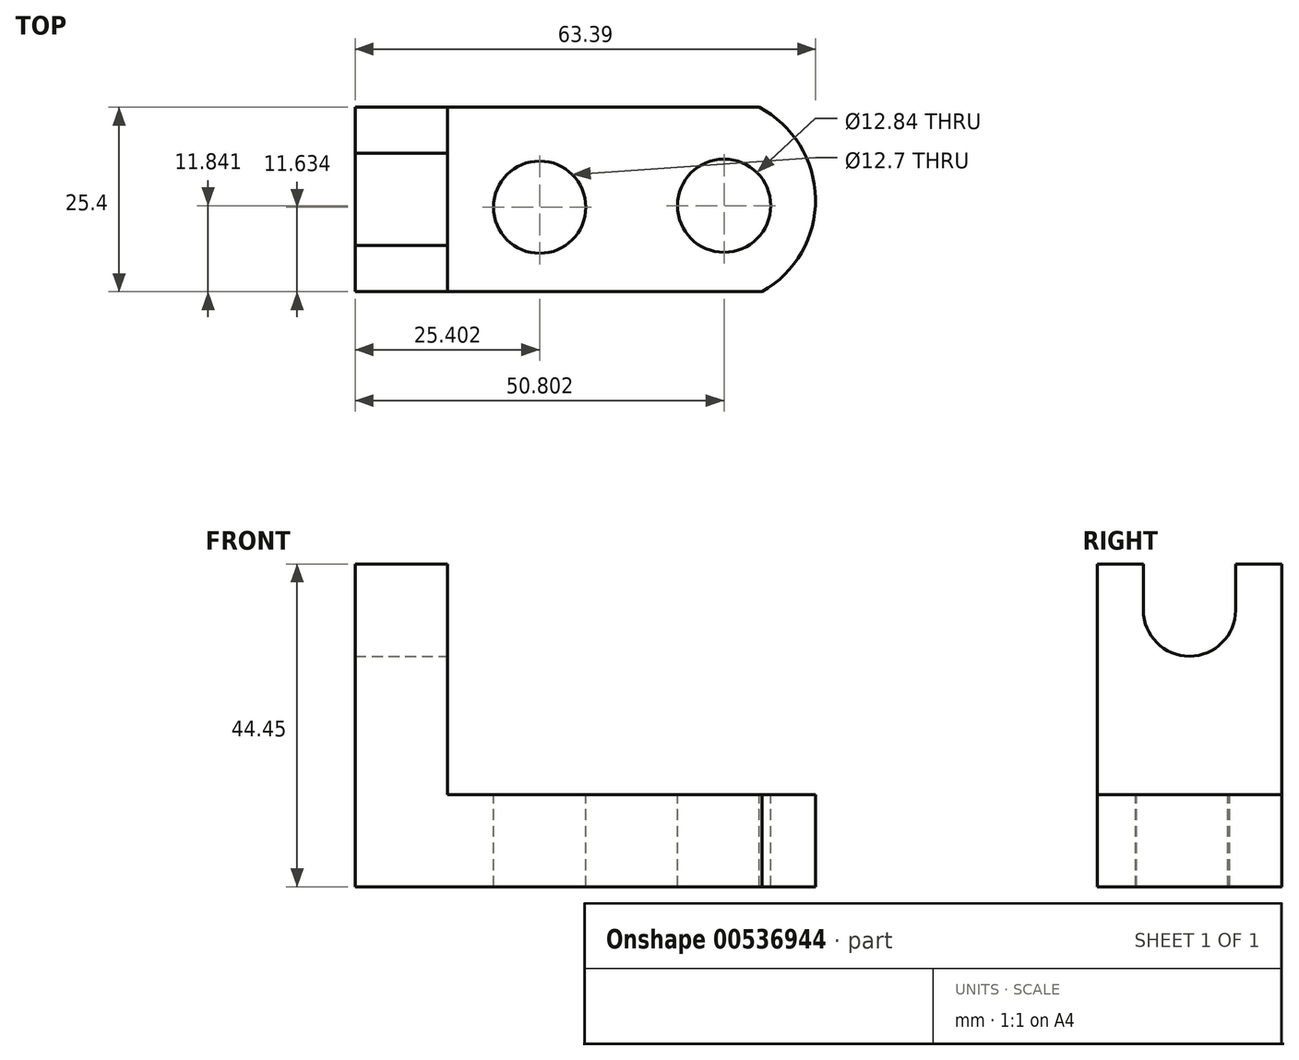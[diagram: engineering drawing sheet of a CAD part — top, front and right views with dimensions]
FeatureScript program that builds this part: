
annotation { "Feature Type Name" : "Feature", "Feature Type Description" : "" }
export const myFeature = defineFeature(function(context is Context, id is Id, definition is map)
    precondition{}
    {
        {
            var Q0;
            Q0=qCreatedBy(makeId("Front.planeOp"),FACE);
            var sketch = newSketch(context, id + "F0", { "sketchPlane" : qUnion([Q0])});
            skLineSegment(sketch, "E0.bottom", {"start": v(-62.54, 0) * mm, "end": v(-49.84, 0) * mm});
            skLineSegment(sketch, "E0.top", {"start": v(-62.54, 44.45) * mm, "end": v(-49.84, 44.45) * mm});
            skLineSegment(sketch, "E0.left", {"start": v(-62.54, 0) * mm, "end": v(-62.54, 44.45) * mm});
            skLineSegment(sketch, "E0.right", {"start": v(-49.84, 0) * mm, "end": v(-49.84, 44.45) * mm});
            skLineSegment(sketch, "E1.bottom", {"start": v(-49.84, 12.7) * mm, "end": v(0.96, 12.7) * mm});
            skLineSegment(sketch, "E1.top", {"start": v(-49.84, 0) * mm, "end": v(0.96, 0) * mm});
            skLineSegment(sketch, "E1.left", {"start": v(-49.84, 12.7) * mm, "end": v(-49.84, 0) * mm});
            skLineSegment(sketch, "E1.right", {"start": v(0.96, 12.7) * mm, "end": v(0.96, 0) * mm});
            skSolve(sketch);
        }
        {
            var Q0;
            Q0 = qSketchRegion(id + "F0", true);
            extrude(context, id + "F1", {"entities" : qUnion([Q0]), "depth" : 25.4 * mm, "offsetDistance" : 25.4 * mm});
        }
        {
            var Q0;
            Q0=makeQuery(id+"F1.opExtrude","SWEPT_FACE",FACE,{"disambiguationData":[OSD([sQuery(id+"F0.wireOp",EDGE,"E0.right")])]});
            var sketch = newSketch(context, id + "F2", { "sketchPlane" : qUnion([Q0])});
            skLineSegment(sketch, "E2", {"start": v(-19.05, 44.45) * mm, "end": v(-19.05, 38.1) * mm});
            skLineSegment(sketch, "E3", {"start": v(-19.05, 38.1) * mm, "end": v(-6.35, 38.1) * mm});
            skLineSegment(sketch, "E4", {"start": v(-6.35, 38.1) * mm, "end": v(-6.35, 44.45) * mm});
            skLineSegment(sketch, "E5", {"start": v(-6.35, 44.45) * mm, "end": v(-19.05, 44.45) * mm});
            skArc(sketch, "E6", {"start": v(-19.05, 38.1) * mm, "mid": v(-12.7, 31.75) * mm, "end": v(-6.35, 38.1) * mm});
            skSolve(sketch);
        }
        {
            var Q0;
            Q0 = qSketchRegion(id + "F2", true);
            extrude(context, id + "F3", {"entities" : qUnion([Q0]), "operationType" : NewBodyOperationType.REMOVE, "oppositeDirection" : true, "depth" : 25.4 * mm, "offsetDistance" : 25.4 * mm});
        }
        {
            var Q0;
            Q0=makeQuery(id+"F1.opExtrude","SWEPT_FACE",FACE,{"disambiguationData":[OSD([sQuery(id+"F0.wireOp",EDGE,"E1.bottom")])]});
            var sketch = newSketch(context, id + "F4", { "sketchPlane" : qUnion([Q0])});
            skCircle(sketch, "E7", {"center": v(-37.14, -13.77) * mm, "radius": 6.35 * mm});
            skCircle(sketch, "E8", {"center": v(-11.74, -13.56) * mm, "radius": 6.42 * mm});
            skArc(sketch, "E9", {"start": v(-6.51, -25.4) * mm, "mid": v(0.85, -12.58) * mm, "end": v(-6.93, 0) * mm});
            skSolve(sketch);
        }
        {
            var Q0;
            Q0 = qSketchRegion(id + "F4", true);
            var Q1;
            {var subQ0=sQuery(id+"F4.wireOp",EDGE,"E9");Q1=makeQuery(id+"F4.imprint","IMPRINT",FACE,{"disambiguationData":[TD([[makeQuery(id+"F4.imprint","IMPRINT",EDGE,{"derivedFrom":subQ0}),-1.0]])]});}
            extrude(context, id + "F5", {"entities" : qUnion([Q0, Q1]), "operationType" : NewBodyOperationType.REMOVE, "oppositeDirection" : true, "depth" : 25.4 * mm, "offsetDistance" : 25.4 * mm});
        }
    });
